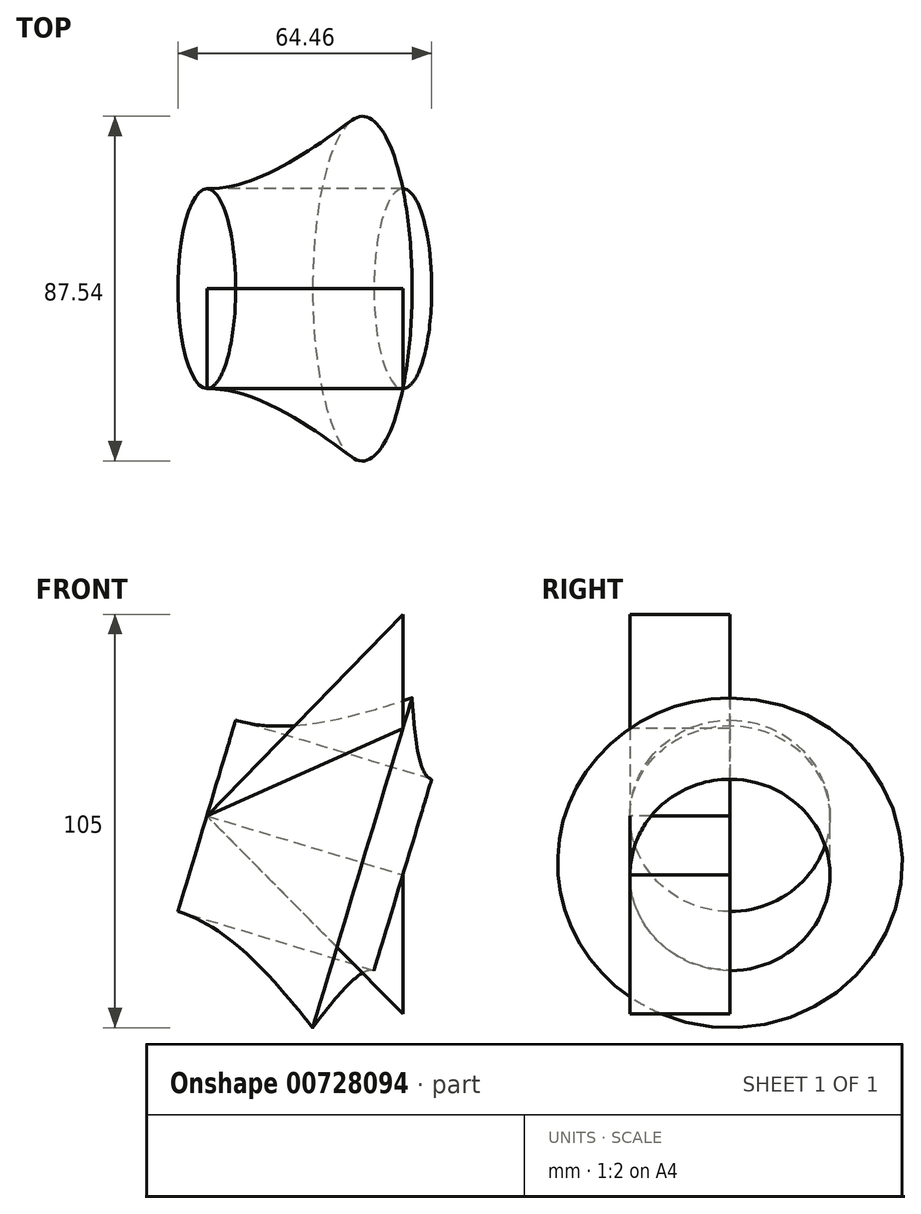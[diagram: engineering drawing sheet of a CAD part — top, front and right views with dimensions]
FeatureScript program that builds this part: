
annotation { "Feature Type Name" : "Feature", "Feature Type Description" : "" }
export const myFeature = defineFeature(function(context is Context, id is Id, definition is map)
    precondition{}
    {
        {
            var Q0;
            Q0=qCreatedBy(makeId("Front.planeOp"),FACE);
            var sketch = newSketch(context, id + "F0", { "sketchPlane" : qUnion([Q0])});
            skLineSegment(sketch, "E0", {"start": v(0, 0) * mm, "end": v(49.8, 51.18) * mm});
            skLineSegment(sketch, "E1", {"start": v(49.8, 51.18) * mm, "end": v(49.8, -50.29) * mm});
            skLineSegment(sketch, "E2", {"start": v(49.8, -50.29) * mm, "end": v(0, 0) * mm});
            skLineSegment(sketch, "E3", {"start": v(49.8, 22.22) * mm, "end": v(0, 0) * mm});
            skLineSegment(sketch, "E4", {"start": v(0, 0) * mm, "end": v(49.8, -15.01) * mm});
            skSolve(sketch);
        }
        {
            var Q0;
            {var subQ0=sQuery(id+"F0.wireOp",EDGE,"E3");Q0=makeQuery(id+"F0.imprint","IMPRINT",FACE,{"disambiguationData":[TD([[makeQuery(id+"F0.imprint","IMPRINT",EDGE,{"derivedFrom":subQ0}),1.0]])]});}
            var sketch = newSketch(context, id + "F1", { "sketchPlane" : qUnion([Q0])});
            skSolve(sketch);
        }
        {
            var Q0;
            {var subQ0=sQuery(id+"F0.wireOp",EDGE,"E2");Q0=makeQuery(id+"F0.imprint","IMPRINT",FACE,{"disambiguationData":[TD([[makeQuery(id+"F0.imprint","IMPRINT",EDGE,{"derivedFrom":subQ0}),-1.0]])]});}
            var Q1;
            {var subQ0=sQuery(id+"F0.wireOp",EDGE,"E0");Q1=makeQuery(id+"F0.imprint","IMPRINT",FACE,{"disambiguationData":[TD([[makeQuery(id+"F0.imprint","IMPRINT",EDGE,{"derivedFrom":subQ0}),-1.0]])]});}
            extrude(context, id + "F2", {"entities" : qUnion([Q0, Q1]), "oppositeDirection" : true, "depth" : 25.4 * mm, "offsetDistance" : 25.4 * mm});
        }
        {
            var Q0;
            {var subQ0=sQuery(id+"F0.wireOp",EDGE,"E3");Q0=makeQuery(id+"F1.imprint","IMPRINT",FACE,{"disambiguationData":[TD([[makeQuery(id+"F1.imprint","IMPRINT",EDGE,{"derivedFrom":makeQuery(id+"F0.imprint","IMPRINT",EDGE,{"derivedFrom":subQ0})}),1.0]])]});}
            var Q1;
            Q1=makeQuery(id+"F2.opExtrude","CAP_EDGE",EDGE,{"disambiguationData":[OSD([sQuery(id+"F0.wireOp",EDGE,"E4")])],"isStart":false});
            revolve(context, id + "F3", {"surfaceOperationType" : NewSurfaceOperationType.NEW, "entities" : qUnion([Q0]), "axis" : qUnion([Q1]), "revolveType" : RevolveType.FULL});
        }
    });
